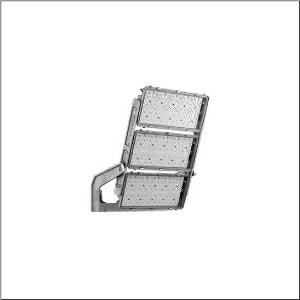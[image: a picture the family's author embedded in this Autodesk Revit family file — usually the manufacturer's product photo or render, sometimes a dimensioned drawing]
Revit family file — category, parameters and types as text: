
# Revit family: floodlight_fl_11_maxi_pro_remote___pl43_5xa779524a01aa_32ee
name_source: partatom
category: Lighting Fixtures
units: mm (PartAtom-declared; Revit-internal decimal feet)

## family parameters
Cut with Voids When Loaded = No
Host = Face
Light Source = No
Part Type = Normal
Room Calculation Point = No
Round Connector Dimension = Use Diameter
Shared = No

## types (1)
- --- (1 x LED, 130000 lm, 1334.7 W, 5700K)
    Apparent Load = 1335 VA
    CIE Flux Codes = 25 74 99 100 100
    Color Rendering = 90
    Color Temperature = 5700K
    Default Elevation = 1800 mm
    Description = Floodlight FL 11  maxi  pro Remote floodlight; light control with lens of PMMA; cover panel of toughened safety glass, transparent; light distribution: PL43, asymmetric direct distribution, LEDcolour temperature: 5700K, rated luminous flux: 130.000lm, colour rendering: CRI > 90, light colour: 957; luminous efficacy: 97lm/W; brightness control: DMX+RDM; with terminal, 8-pole, max. 2.5mm², mains connection: 220..240V/380..400V AC, 50/60Hz, surge voltage resistance: line to ground: 10kV, ECG replaceable separately, no afterglow with DALI off / DMX off command, LED unit replaceable without ESD environment, dustproof LED module, dimming range 10..100%; 1335W reduction: 534W; floodlight with 3x LED unit of diecast aluminium, coated grey; length: 713mm / width: 651mm / height: 338mm; housing frame, of diecast aluminium, uncoated, natural, mounting bracket, of diecast aluminium, uncoated, natural, equipment: Power, protection rating (complete): IP66; insulation class (complete): insulation class I (protective earthing); certification: CE, ENEC, VDE; ball protection: ball impact resistance with accessories, only for outdoor installations, rated ambient temperature 10°C, permissible operating ambient temperature: -40..+30°C, permissible storage temperature: -40..+85°C; packaging unit: 1 piece

Light Distribution: PL43
    Height = 320 mm
    Lamp = 1 x LED
    Lamp Light Flux = 130000 lm
    Lamp Power = 1334.7 W
    Lamp count = 1
    Length = 1002 mm
    Luminous efficacy = 97 lm/W
    Manufacturer = Siteco
    ModVariant = No
    Model = 5XA779524A01AA
    Number of Poles = 1
    OnlyDefault = Yes
    Power Factor = 1
    Product Name = Floodlight FL 11 maxi pro Remote | PL43
    Product group = floodlight | pylon top
    ProductGroupID = 6101
    Protection Class = Protection class I
    Protection Degree = IP 66
    RLX_Detail_Level = 1
    RlxData = <blob elided: 52485 chars, md5=ca41dfee>
    Socket = socket
    Standby Power = 0 W
    System Light Flux = 130000 lm
    System Power = 1335 W
    Type Comments = factory setting: luminous flux: 100 % | dim-lin: 255 | 920 mA
    Type Image = l_1006784.jpg
    URL = http://relux.com
    VarID = @adj_006161
    Voltage = 0 V
    Weight = 0.00 kg
    Width = 655 mm

## geometry (parser evidence)
native form markers: Blend x4, Sweep x14
no freeform markers — native parametric forms only
